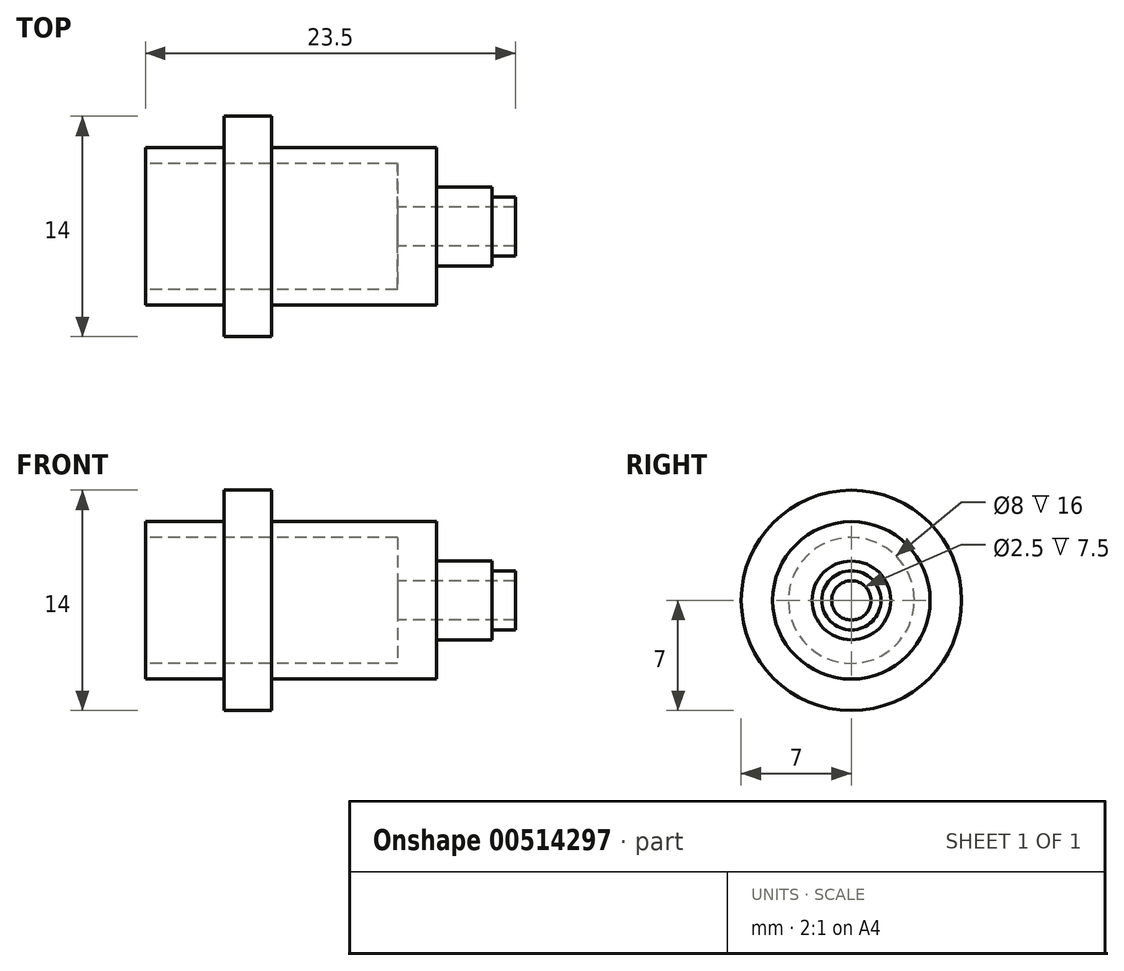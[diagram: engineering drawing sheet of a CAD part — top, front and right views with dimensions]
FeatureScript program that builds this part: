
annotation { "Feature Type Name" : "Feature", "Feature Type Description" : "" }
export const myFeature = defineFeature(function(context is Context, id is Id, definition is map)
    precondition{}
    {
        {
            var Q0;
            Q0=qCreatedBy(makeId("Top.planeOp"),FACE);
            var sketch = newSketch(context, id + "F0", { "sketchPlane" : qUnion([Q0])});
            skLineSegment(sketch, "E0", {"start": v(-18.5, 0) * mm, "end": v(-18.5, 5) * mm});
            skLineSegment(sketch, "E1", {"start": v(-18.5, 5) * mm, "end": v(-13.5, 5) * mm});
            skLineSegment(sketch, "E2", {"start": v(3.5, 2.5) * mm, "end": v(3.5, 1.87) * mm});
            skLineSegment(sketch, "E3", {"start": v(3.5, 1.87) * mm, "end": v(5, 1.87) * mm});
            skLineSegment(sketch, "E4", {"start": v(5, 1.87) * mm, "end": v(5, 0) * mm});
            skLineSegment(sketch, "E5", {"start": v(0, 5) * mm, "end": v(0, 2.5) * mm});
            skLineSegment(sketch, "E6", {"start": v(0, 2.5) * mm, "end": v(3.5, 2.5) * mm});
            skLineSegment(sketch, "E7.MirrorCS", {"start": v(3.5, -1.87) * mm, "end": v(5, -1.87) * mm});
            skLineSegment(sketch, "E8.MirrorCS", {"start": v(5, -1.87) * mm, "end": v(5, 0) * mm});
            skLineSegment(sketch, "E9.MirrorCS", {"start": v(3.5, -2.5) * mm, "end": v(3.5, -1.87) * mm});
            skLineSegment(sketch, "E10.MirrorCS", {"start": v(-18.5, 0) * mm, "end": v(-18.5, -5) * mm});
            skLineSegment(sketch, "E11.MirrorCS", {"start": v(-18.5, -5) * mm, "end": v(-13.5, -5) * mm});
            skLineSegment(sketch, "E12.MirrorCS", {"start": v(0, -2.5) * mm, "end": v(3.5, -2.5) * mm});
            skLineSegment(sketch, "E13.MirrorCS", {"start": v(0, -5) * mm, "end": v(0, -2.5) * mm});
            skLineSegment(sketch, "E14", {"start": v(-18.5, 0) * mm, "end": v(5, 0) * mm, "construction": true});
            skLineSegment(sketch, "E15", {"start": v(-10.5, 5) * mm, "end": v(-10.5, 7) * mm});
            skLineSegment(sketch, "E16", {"start": v(-13.5, 7) * mm, "end": v(-10.5, 7) * mm});
            skLineSegment(sketch, "E17", {"start": v(-13.5, 7) * mm, "end": v(-13.5, 5) * mm});
            skLineSegment(sketch, "E18.trimOffspring", {"start": v(-10.5, 5) * mm, "end": v(0, 5) * mm});
            skLineSegment(sketch, "E19.MirrorCS", {"start": v(-13.5, -7) * mm, "end": v(-13.5, -5) * mm});
            skLineSegment(sketch, "E20.MirrorCS", {"start": v(-13.5, -7) * mm, "end": v(-10.5, -7) * mm});
            skLineSegment(sketch, "E21.MirrorCS", {"start": v(-10.5, -5) * mm, "end": v(-10.5, -7) * mm});
            skLineSegment(sketch, "E22.trimOffspring", {"start": v(-10.5, -5) * mm, "end": v(0, -5) * mm});
            skLineSegment(sketch, "E23", {"start": v(-18.5, 4) * mm, "end": v(-2.5, 4) * mm});
            skLineSegment(sketch, "E24", {"start": v(-2.5, 4) * mm, "end": v(-2.5, 1.25) * mm});
            skLineSegment(sketch, "E25", {"start": v(-2.5, 1.25) * mm, "end": v(5, 1.25) * mm});
            skSolve(sketch);
        }
        {
            var Q0;
            Q0=makeQuery(id+"F0.imprint","IMPRINT",FACE,{"disambiguationData":[TD([[makeQuery(id+"F0.imprint","IMPRINT",EDGE,{"derivedFrom":sQuery(id+"F0.wireOp",EDGE,"E0")}),-1.0]])]});
            var Q1;
            {var subQ3=sQuery(id+"F0.wireOp",EDGE,"E1");Q1=makeQuery(id+"F0.imprint","IMPRINT",FACE,{"disambiguationData":[TD([[makeQuery(id+"F0.imprint","IMPRINT",EDGE,{"derivedFrom":subQ3}),-1.0]])]});}
            var Q2;
            Q2=sQuery(id+"F0.wireOp",EDGE,"E14");
            revolve(context, id + "F1", {"entities" : qUnion([Q0, Q1]), "axis" : qUnion([Q2]), "revolveType" : RevolveType.FULL});
        }
    });
